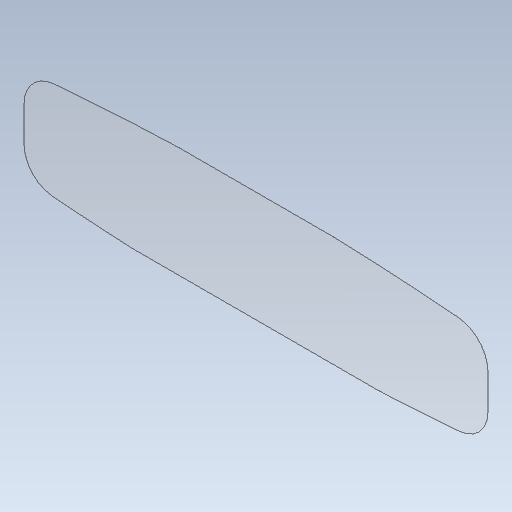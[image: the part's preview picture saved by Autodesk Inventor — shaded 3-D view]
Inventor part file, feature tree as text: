
AUTODESK INVENTOR PART (.ipt)
format: ipt  version: 2021 (Build 250183000, 183)  size: 130,048 bytes
history: native  units: in
note: dims shown in document units (in); Inventor stores cm internally (conversion verified against a paired STEP export)
features: other x3, extrude x1, sketch x1
ambient origin geometry x8: Origin, YZ Plane, XZ Plane, XY Plane, X Axis, Y Axis, Z Axis, Center Point
bodies: Solid1 (feature_tree)
feature tree (5):
  other  "Blocks"
  extrude  "Extrusion1"  Depth=0.0197in
  sketch  "Sketch1"  dims[d0=23.622in d1=4.7244in d2=4.7244in d3=5.5118in d4=5.5118in d5=7.874in d6=7.874in d7=7.874in d8=12.5984in d9=5.6299in d10=0.3937in d11=0.3937in d12=0.5118in d13=0.5118in d14=1.6535in d15=1.5748in d16=1.5748in d17=1.6535in d18=0.7874in d19=11.811in d20=2.9528in d21=0.0197in d22=0.0in]
  other  "Clock Front Face Outline"
  other  "Clock Front Face Outline:1"
